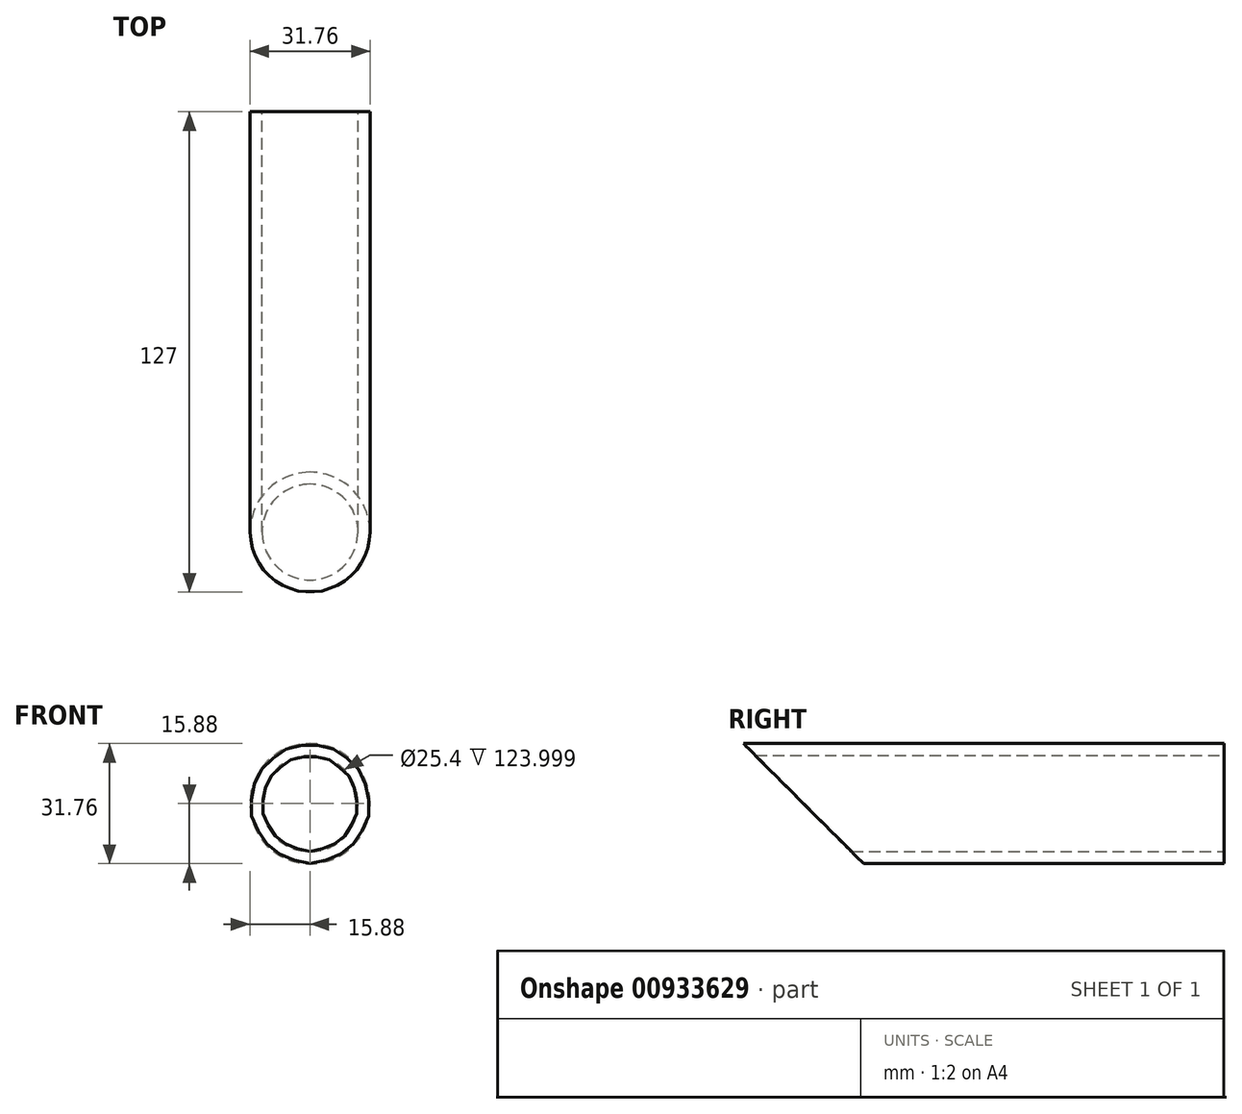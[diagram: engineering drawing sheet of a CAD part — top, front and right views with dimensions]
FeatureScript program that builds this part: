
annotation { "Feature Type Name" : "Feature", "Feature Type Description" : "" }
export const myFeature = defineFeature(function(context is Context, id is Id, definition is map)
    precondition{}
    {
        {
            var Q0;
            Q0=qCreatedBy(makeId("Front.planeOp"),FACE);
            var sketch = newSketch(context, id + "F0", { "sketchPlane" : qUnion([Q0])});
            skCircle(sketch, "E0", {"center": v(0, 0) * mm, "radius": 12.7 * mm});
            skCircle(sketch, "E1", {"center": v(0, 0) * mm, "radius": 15.88 * mm});
            skSolve(sketch);
        }
        {
            var Q0;
            Q0=makeQuery(id+"F0.imprint","IMPRINT",FACE,{"disambiguationData":[TD([[makeQuery(id+"F0.imprint","IMPRINT",EDGE,{"derivedFrom":sQuery(id+"F0.wireOp",EDGE,"E0")}),-1.0]])]});
            extrude(context, id + "F1", {"entities" : qUnion([Q0]), "depth" : 127 * mm, "offsetDistance" : 25.4 * mm});
        }
        {
            var Q0;
            Q0=qCreatedBy(makeId("Front.planeOp"),FACE);
            cPlane(context, id + "F2", {"entities" : qUnion([Q0]), "cplaneType" : CPlaneType.OFFSET, "offset" : 111.12 * mm, "width" : 152.4 * mm, "height" : 152.4 * mm});
        }
        {
            var Q0;
            Q0=qCreatedBy(id+"F2.planeOp",FACE);
            var sketch = newSketch(context, id + "F3", { "sketchPlane" : qUnion([Q0])});
            skLineSegment(sketch, "E2", {"start": v(-88.39, 0) * mm, "end": v(86.14, 0) * mm});
            skSolve(sketch);
        }
        {
            var Q0;
            Q0=qCreatedBy(id+"F2.planeOp",FACE);
            var Q1;
            Q1=sQuery(id+"F3.wireOp",EDGE,"E2");
            cPlane(context, id + "F4", {"entities" : qUnion([Q0, Q1]), "cplaneType" : CPlaneType.LINE_ANGLE, "offset" : 25.4 * mm, "angle" : 45 * degree, "width" : 152.4 * mm, "height" : 152.4 * mm});
        }
        {
            var Q0;
            Q0=qCreatedBy(id+"F4.planeOp",FACE);
            var sketch = newSketch(context, id + "F5", { "sketchPlane" : qUnion([Q0])});
            skLineSegment(sketch, "E3.bottom", {"start": v(76.83, 143.25) * mm, "end": v(-83.77, 143.25) * mm});
            skLineSegment(sketch, "E3.top", {"start": v(76.83, 31.68) * mm, "end": v(-83.77, 31.68) * mm});
            skLineSegment(sketch, "E3.left", {"start": v(76.83, 143.25) * mm, "end": v(76.83, 31.68) * mm});
            skLineSegment(sketch, "E3.right", {"start": v(-83.77, 143.25) * mm, "end": v(-83.77, 31.68) * mm});
            skSolve(sketch);
        }
        {
            var Q0;
            Q0=makeQuery(id+"F5.imprint","IMPRINT",FACE,{"disambiguationData":[TD([[makeQuery(id+"F5.imprint","IMPRINT",EDGE,{"derivedFrom":sQuery(id+"F5.wireOp",EDGE,"E3.bottom")}),1.0]])]});
            extrude(context, id + "F6", {"entities" : qUnion([Q0]), "operationType" : NewBodyOperationType.REMOVE, "oppositeDirection" : true, "depth" : 25.4 * mm, "offsetDistance" : 25.4 * mm});
        }
    });
